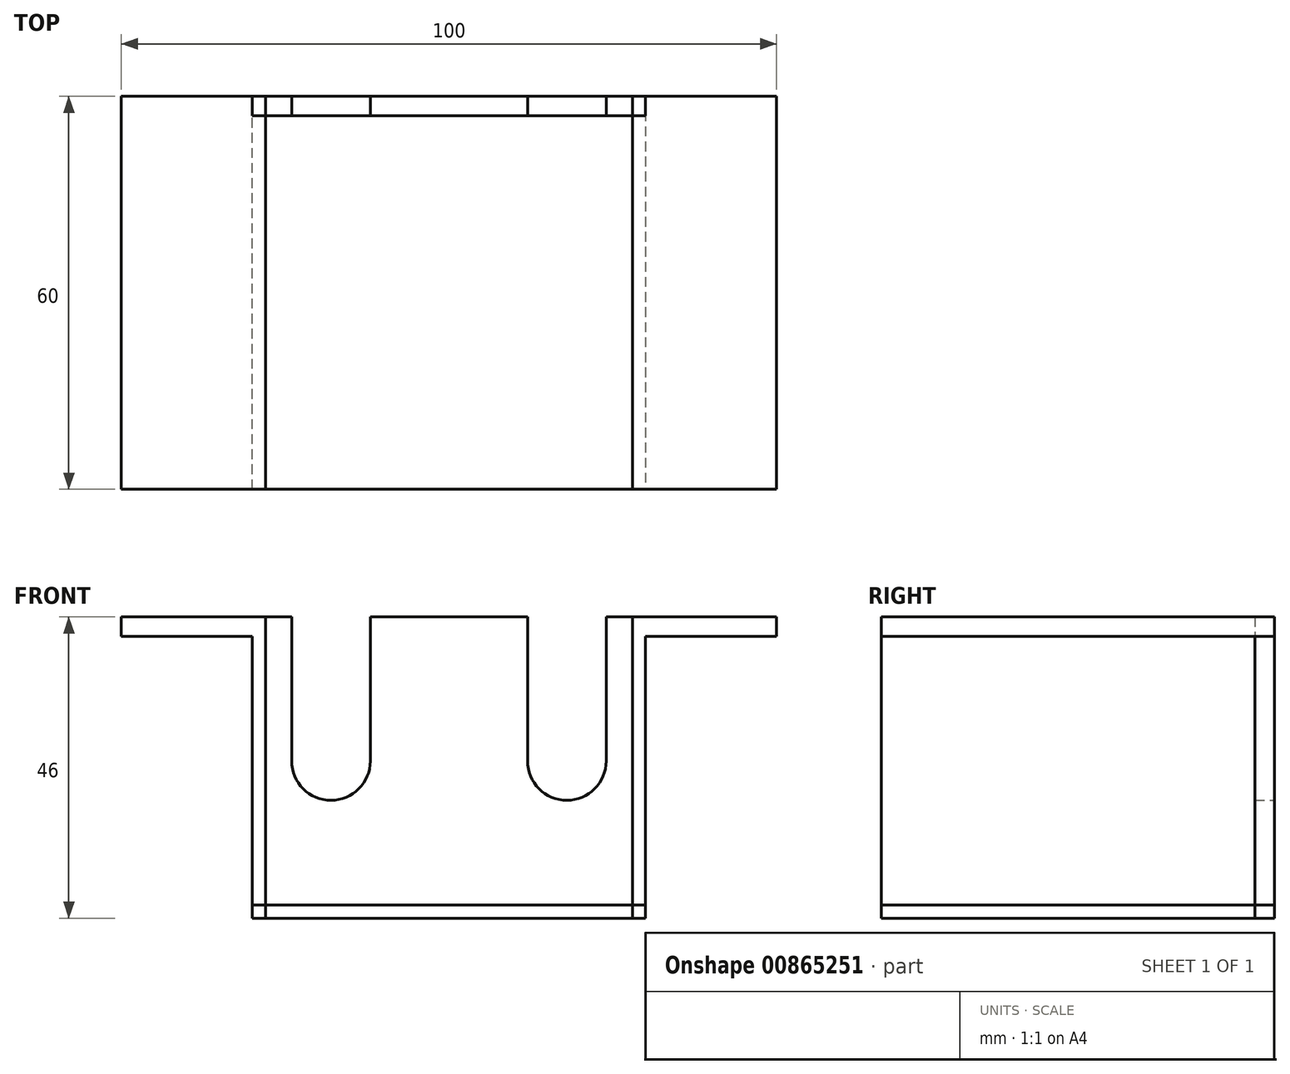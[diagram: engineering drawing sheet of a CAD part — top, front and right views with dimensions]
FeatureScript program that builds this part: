
annotation { "Feature Type Name" : "Feature", "Feature Type Description" : "" }
export const myFeature = defineFeature(function(context is Context, id is Id, definition is map)
    precondition{}
    {
        {
            var Q0;
            Q0=qCreatedBy(makeId("Top.planeOp"),FACE);
            var sketch = newSketch(context, id + "F0", { "sketchPlane" : qUnion([Q0])});
            skLineSegment(sketch, "E0.bottom", {"start": v(0, 0) * mm, "end": v(60, 0) * mm});
            skLineSegment(sketch, "E0.top", {"start": v(0, 60) * mm, "end": v(60, 60) * mm});
            skLineSegment(sketch, "E0.left", {"start": v(0, 0) * mm, "end": v(0, 60) * mm});
            skLineSegment(sketch, "E0.right", {"start": v(60, 0) * mm, "end": v(60, 60) * mm});
            skLineSegment(sketch, "E1", {"start": v(0, 0) * mm, "end": v(2, 0) * mm});
            skLineSegment(sketch, "E2", {"start": v(2, 0) * mm, "end": v(4.78, 0) * mm});
            skLineSegment(sketch, "E3", {"start": v(2, 0) * mm, "end": v(2, 60) * mm});
            skLineSegment(sketch, "E4", {"start": v(60, 0) * mm, "end": v(58, 0) * mm});
            skLineSegment(sketch, "E5", {"start": v(58, 0) * mm, "end": v(58, 60) * mm});
            skSolve(sketch);
        }
        {
            var Q0;
            {var subQ0=sQuery(id+"F0.wireOp",EDGE,"E0.left");Q0=makeQuery(id+"F0.imprint","IMPRINT",FACE,{"disambiguationData":[TD([[makeQuery(id+"F0.imprint","IMPRINT",EDGE,{"derivedFrom":subQ0}),-1.0]])]});}
            var Q1;
            {var subQ0=sQuery(id+"F0.wireOp",EDGE,"E0.right");Q1=makeQuery(id+"F0.imprint","IMPRINT",FACE,{"disambiguationData":[TD([[makeQuery(id+"F0.imprint","IMPRINT",EDGE,{"derivedFrom":subQ0}),1.0]])]});}
            extrude(context, id + "F1", {"entities" : qUnion([Q0, Q1]), "depth" : 46 * mm, "offsetDistance" : 25 * mm});
        }
        {
            var Q0;
            Q0 = qSketchRegion(id + "F0", true);
            extrude(context, id + "F2", {"entities" : qUnion([Q0]), "depth" : 2 * mm, "offsetDistance" : 25 * mm});
        }
        {
            var Q0;
            Q0=makeQuery(id+"F1.opExtrude","SWEPT_FACE",FACE,{"disambiguationData":[OSD([sQuery(id+"F0.wireOp",EDGE,"E0.left")])]});
            var sketch = newSketch(context, id + "F3", { "sketchPlane" : qUnion([Q0])});
            skLineSegment(sketch, "E6", {"start": v(0, 46) * mm, "end": v(0, 43) * mm});
            skLineSegment(sketch, "E7", {"start": v(0, 43) * mm, "end": v(-60, 43) * mm});
            skLineSegment(sketch, "E8", {"start": v(-60, 43) * mm, "end": v(-60, 46) * mm});
            skLineSegment(sketch, "E9", {"start": v(-60, 46) * mm, "end": v(0, 46) * mm});
            skSolve(sketch);
        }
        {
            var Q0;
            Q0=makeQuery(id+"F3.imprint","IMPRINT",FACE,{"disambiguationData":[TD([[makeQuery(id+"F3.imprint","IMPRINT",EDGE,{"derivedFrom":sQuery(id+"F3.wireOp",EDGE,"E6")}),-1.0]])]});
            extrude(context, id + "F4", {"entities" : qUnion([Q0]), "operationType" : NewBodyOperationType.ADD, "depth" : 20 * mm, "offsetDistance" : 25 * mm});
        }
        {
            var Q0;
            Q0=makeQuery(id+"F1.opExtrude","SWEPT_FACE",FACE,{"disambiguationData":[OSD([sQuery(id+"F0.wireOp",EDGE,"E0.right")])]});
            var sketch = newSketch(context, id + "F5", { "sketchPlane" : qUnion([Q0])});
            skLineSegment(sketch, "E10", {"start": v(60, 46) * mm, "end": v(60, 43) * mm});
            skLineSegment(sketch, "E11", {"start": v(60, 43) * mm, "end": v(0, 43) * mm});
            skLineSegment(sketch, "E12", {"start": v(0, 43) * mm, "end": v(0, 46) * mm});
            skLineSegment(sketch, "E13", {"start": v(0, 46) * mm, "end": v(60, 46) * mm});
            skSolve(sketch);
        }
        {
            var Q0;
            Q0=makeQuery(id+"F5.imprint","IMPRINT",FACE,{"disambiguationData":[TD([[makeQuery(id+"F5.imprint","IMPRINT",EDGE,{"derivedFrom":sQuery(id+"F5.wireOp",EDGE,"E10")}),-1.0]])]});
            extrude(context, id + "F6", {"entities" : qUnion([Q0]), "operationType" : NewBodyOperationType.ADD, "depth" : 20 * mm, "offsetDistance" : 25 * mm});
        }
        {
            var Q0;
            {var subQ0=sQuery(id+"F0.wireOp",EDGE,"E0.top");Q0=makeQuery(id+"F4.boolean.opBoolean","MERGE",FACE,{"derivedFrom":[makeQuery(id+"F1.opExtrude","SWEPT_FACE",FACE,{"disambiguationData":[OSD([subQ0]),TDD([makeQuery(id+"F0.imprint","IMPRINT",EDGE,{"disambiguationData":[TD([[makeQuery(id+"F0.imprint","INTERSECT",VERTEX,{"derivedFrom":[subQ0,sQuery(id+"F0.wireOp",EDGE,"E0.left")]}),-1.0]])],"derivedFrom":subQ0})])]}),makeQuery(id+"F4.opExtrude","SWEPT_FACE",FACE,{"disambiguationData":[OSD([sQuery(id+"F3.wireOp",EDGE,"E8")])]})]});}
            var sketch = newSketch(context, id + "F7", { "sketchPlane" : qUnion([Q0])});
            skLineSegment(sketch, "E14", {"start": v(0, 0) * mm, "end": v(0, 46) * mm});
            skLineSegment(sketch, "E15", {"start": v(0, 46) * mm, "end": v(-60, 46) * mm});
            skLineSegment(sketch, "E16", {"start": v(-60, 46) * mm, "end": v(-60, 0) * mm});
            skLineSegment(sketch, "E17", {"start": v(0, 0) * mm, "end": v(-60, 0) * mm});
            skSolve(sketch);
        }
        {
            var Q0;
            Q0 = qSketchRegion(id + "F7", true);
            extrude(context, id + "F8", {"entities" : qUnion([Q0]), "oppositeDirection" : true, "depth" : 3 * mm, "offsetDistance" : 25 * mm});
        }
        {
            var Q0;
            Q0=makeQuery(id+"F8.opExtrude","CAP_FACE",FACE,{"disambiguationData":[OSD([sQuery(id+"F7.wireOp",EDGE,"E14"),sQuery(id+"F7.wireOp",EDGE,"E15"),sQuery(id+"F7.wireOp",EDGE,"E16"),sQuery(id+"F7.wireOp",EDGE,"E17")])],"isStart":true});
            var sketch = newSketch(context, id + "F9", { "sketchPlane" : qUnion([Q0])});
            skArc(sketch, "E18", {"start": v(-18, 24) * mm, "mid": v(-12, 18) * mm, "end": v(-6, 24) * mm});
            skArc(sketch, "E19", {"start": v(-54, 24) * mm, "mid": v(-48, 18) * mm, "end": v(-42, 24) * mm});
            skLineSegment(sketch, "E20", {"start": v(-6, 24) * mm, "end": v(-6, 46) * mm});
            skLineSegment(sketch, "E21", {"start": v(-18, 24) * mm, "end": v(-18, 46) * mm});
            skLineSegment(sketch, "E22", {"start": v(-42, 46) * mm, "end": v(-42, 24) * mm});
            skLineSegment(sketch, "E23", {"start": v(-54, 24) * mm, "end": v(-54, 46) * mm});
            skSolve(sketch);
        }
        {
            var Q0;
            Q0=makeQuery(id+"F9.imprint","IMPRINT",FACE,{"disambiguationData":[TD([[makeQuery(id+"F9.imprint","IMPRINT",EDGE,{"derivedFrom":sQuery(id+"F9.wireOp",EDGE,"E18")}),1.0]])]});
            var Q1;
            Q1=makeQuery(id+"F9.imprint","IMPRINT",FACE,{"disambiguationData":[TD([[makeQuery(id+"F9.imprint","IMPRINT",EDGE,{"derivedFrom":sQuery(id+"F9.wireOp",EDGE,"E19")}),1.0]])]});
            extrude(context, id + "F10", {"entities" : qUnion([Q0, Q1]), "operationType" : NewBodyOperationType.REMOVE, "oppositeDirection" : true, "depth" : 3 * mm, "offsetDistance" : 25 * mm});
        }
    });
